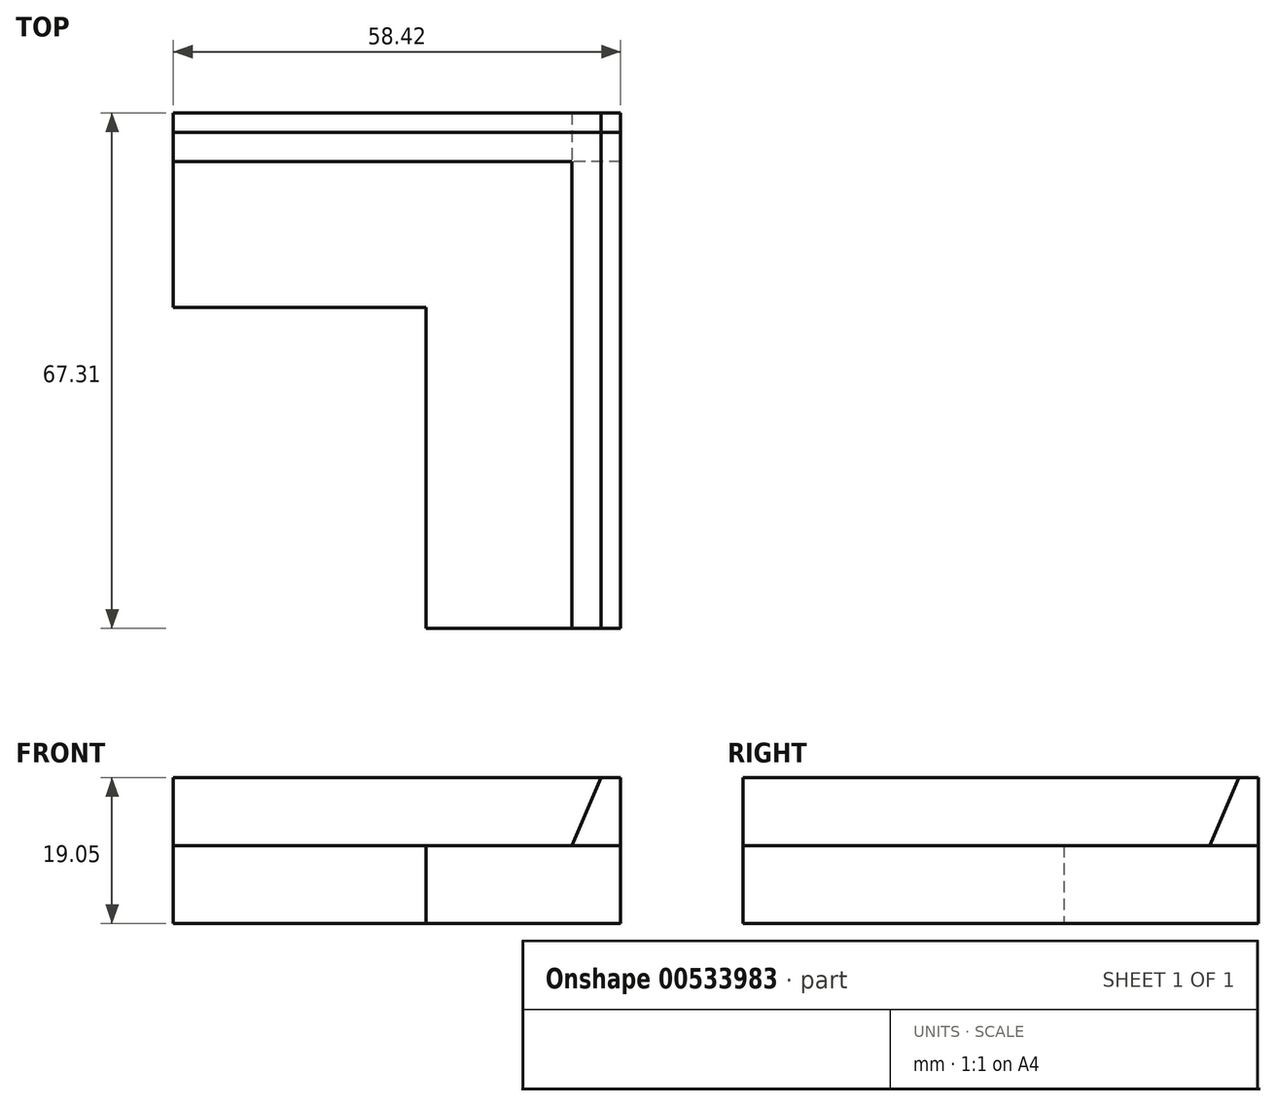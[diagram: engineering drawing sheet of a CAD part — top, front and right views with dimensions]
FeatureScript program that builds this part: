
annotation { "Feature Type Name" : "Feature", "Feature Type Description" : "" }
export const myFeature = defineFeature(function(context is Context, id is Id, definition is map)
    precondition{}
    {
        {
            var Q0;
            Q0=qCreatedBy(makeId("Top.planeOp"),FACE);
            var sketch = newSketch(context, id + "F0", { "sketchPlane" : qUnion([Q0])});
            skLineSegment(sketch, "E0.bottom", {"start": v(0, 0) * mm, "end": v(25.4, 0) * mm});
            skLineSegment(sketch, "E0.top", {"start": v(0, 67.31) * mm, "end": v(25.4, 67.31) * mm});
            skLineSegment(sketch, "E0.left", {"start": v(0, 0) * mm, "end": v(0, 67.3) * mm});
            skLineSegment(sketch, "E0.right", {"start": v(25.4, 0) * mm, "end": v(25.4, 67.31) * mm});
            skLineSegment(sketch, "E1.bottom", {"start": v(0, 67.31) * mm, "end": v(-33.02, 67.31) * mm});
            skLineSegment(sketch, "E1.top", {"start": v(0, 41.91) * mm, "end": v(-33.02, 41.91) * mm});
            skLineSegment(sketch, "E1.left", {"start": v(0, 67.31) * mm, "end": v(0, 41.91) * mm});
            skLineSegment(sketch, "E1.right", {"start": v(-33.02, 67.31) * mm, "end": v(-33.02, 41.91) * mm});
            skSolve(sketch);
        }
        {
            var Q0;
            Q0=makeQuery(id+"F0.imprint","IMPRINT",FACE,{"disambiguationData":[TD([[makeQuery(id+"F0.imprint","IMPRINT",EDGE,{"derivedFrom":sQuery(id+"F0.wireOp",EDGE,"E0.bottom")}),1.0]])]});
            var Q1;
            Q1=makeQuery(id+"F0.imprint","IMPRINT",FACE,{"disambiguationData":[TD([[makeQuery(id+"F0.imprint","IMPRINT",EDGE,{"derivedFrom":sQuery(id+"F0.wireOp",EDGE,"E1.bottom")}),1.0]])]});
            extrude(context, id + "F1", {"entities" : qUnion([Q0, Q1]), "depth" : 10.16 * mm, "offsetDistance" : 25.4 * mm});
        }
        {
            var Q0;
            Q0=makeQuery(id+"F1.opExtrude","SWEPT_FACE",FACE,{"disambiguationData":[OSD([sQuery(id+"F0.wireOp",EDGE,"E0.bottom")])]});
            var sketch = newSketch(context, id + "F2", { "sketchPlane" : qUnion([Q0])});
            skLineSegment(sketch, "E2", {"start": v(25.4, 10.16) * mm, "end": v(25.4, 19.05) * mm});
            skLineSegment(sketch, "E3", {"start": v(25.4, 19.05) * mm, "end": v(22.86, 19.05) * mm});
            skLineSegment(sketch, "E4", {"start": v(25.4, 10.16) * mm, "end": v(19.05, 10.16) * mm});
            skLineSegment(sketch, "E5", {"start": v(22.86, 19.05) * mm, "end": v(19.05, 10.16) * mm});
            skSolve(sketch);
        }
        {
            var Q0;
            Q0 = qSketchRegion(id + "F2", true);
            extrude(context, id + "F3", {"entities" : qUnion([Q0]), "oppositeDirection" : true, "depth" : 67.3 * mm, "offsetDistance" : 25.4 * mm});
        }
        {
            var Q0;
            Q0=makeQuery(id+"F1.opExtrude","SWEPT_FACE",FACE,{"disambiguationData":[OSD([sQuery(id+"F0.wireOp",EDGE,"E1.right")])]});
            var sketch = newSketch(context, id + "F4", { "sketchPlane" : qUnion([Q0])});
            skLineSegment(sketch, "E6", {"start": v(-67.31, 10.16) * mm, "end": v(-67.31, 19.05) * mm});
            skLineSegment(sketch, "E7", {"start": v(-67.31, 19.05) * mm, "end": v(-64.77, 19.05) * mm});
            skLineSegment(sketch, "E8", {"start": v(-67.31, 10.16) * mm, "end": v(-60.96, 10.16) * mm});
            skLineSegment(sketch, "E9", {"start": v(-60.96, 10.16) * mm, "end": v(-64.77, 19.05) * mm});
            skSolve(sketch);
        }
        {
            var Q0;
            Q0=makeQuery(id+"F4.imprint","IMPRINT",FACE,{"disambiguationData":[TD([[makeQuery(id+"F4.imprint","IMPRINT",EDGE,{"derivedFrom":sQuery(id+"F4.wireOp",EDGE,"E6")}),-1.0]])]});
            extrude(context, id + "F5", {"entities" : qUnion([Q0]), "oppositeDirection" : true, "depth" : 58.42 * mm, "offsetDistance" : 25.4 * mm});
        }
    });
